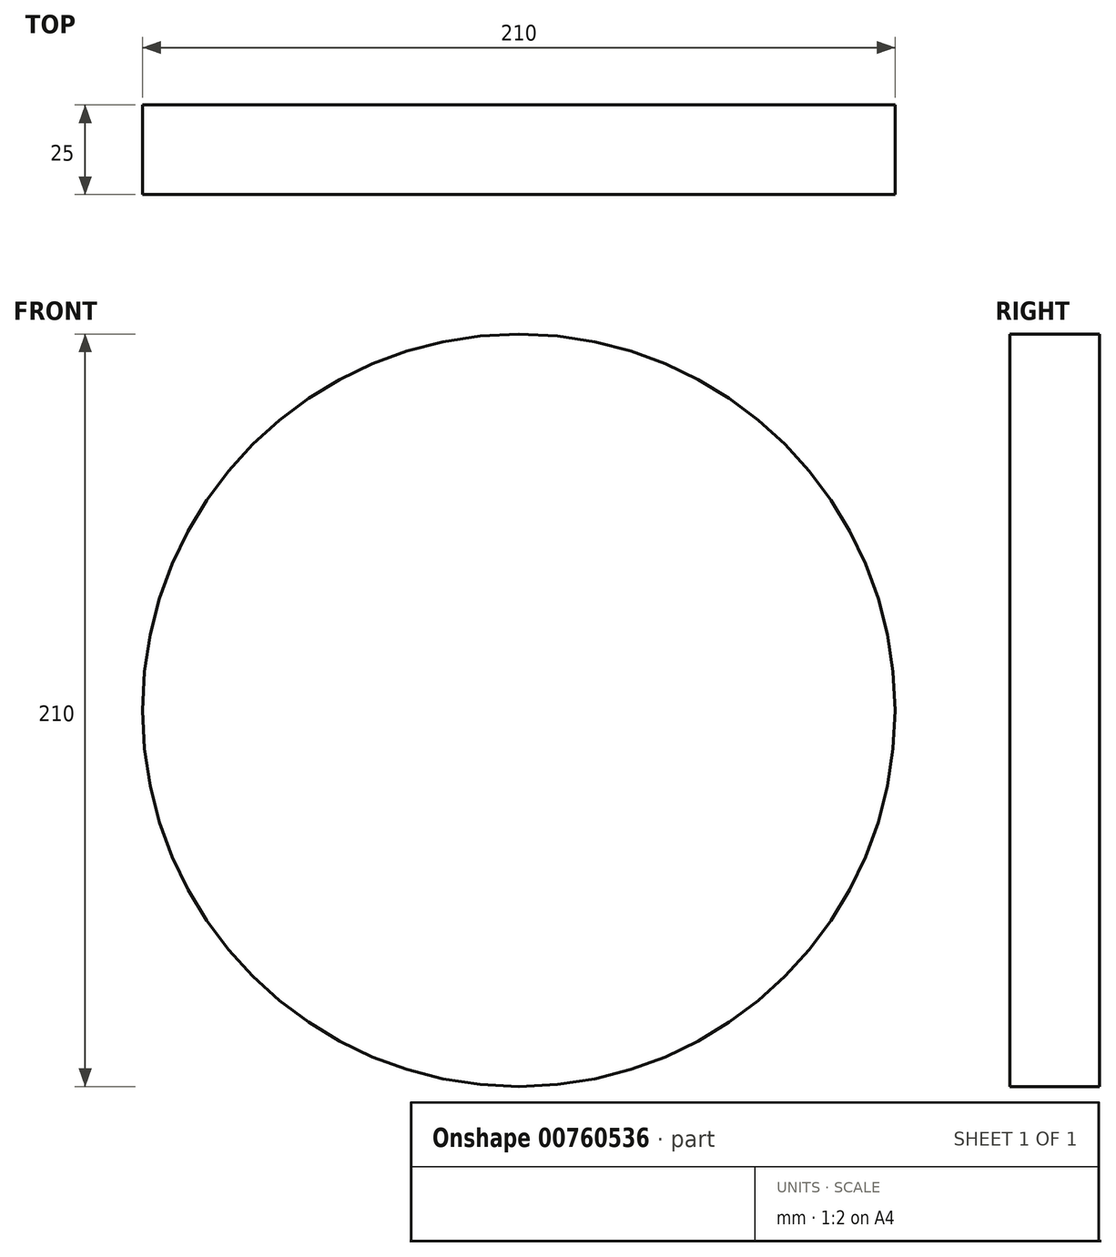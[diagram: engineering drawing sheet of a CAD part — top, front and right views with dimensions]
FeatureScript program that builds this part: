
annotation { "Feature Type Name" : "Feature", "Feature Type Description" : "" }
export const myFeature = defineFeature(function(context is Context, id is Id, definition is map)
    precondition{}
    {
        {
            var Q0;
            Q0=qCreatedBy(makeId("Front.planeOp"),FACE);
            var sketch = newSketch(context, id + "F0", { "sketchPlane" : qUnion([Q0])});
            skCircle(sketch, "E0", {"center": v(0, 0) * mm, "radius": 105 * mm});
            skSolve(sketch);
        }
        {
            var Q0;
            Q0 = qSketchRegion(id + "F0", true);
            extrude(context, id + "F1", {"entities" : qUnion([Q0]), "depth" : 25 * mm, "offsetDistance" : 25 * mm});
        }
    });
